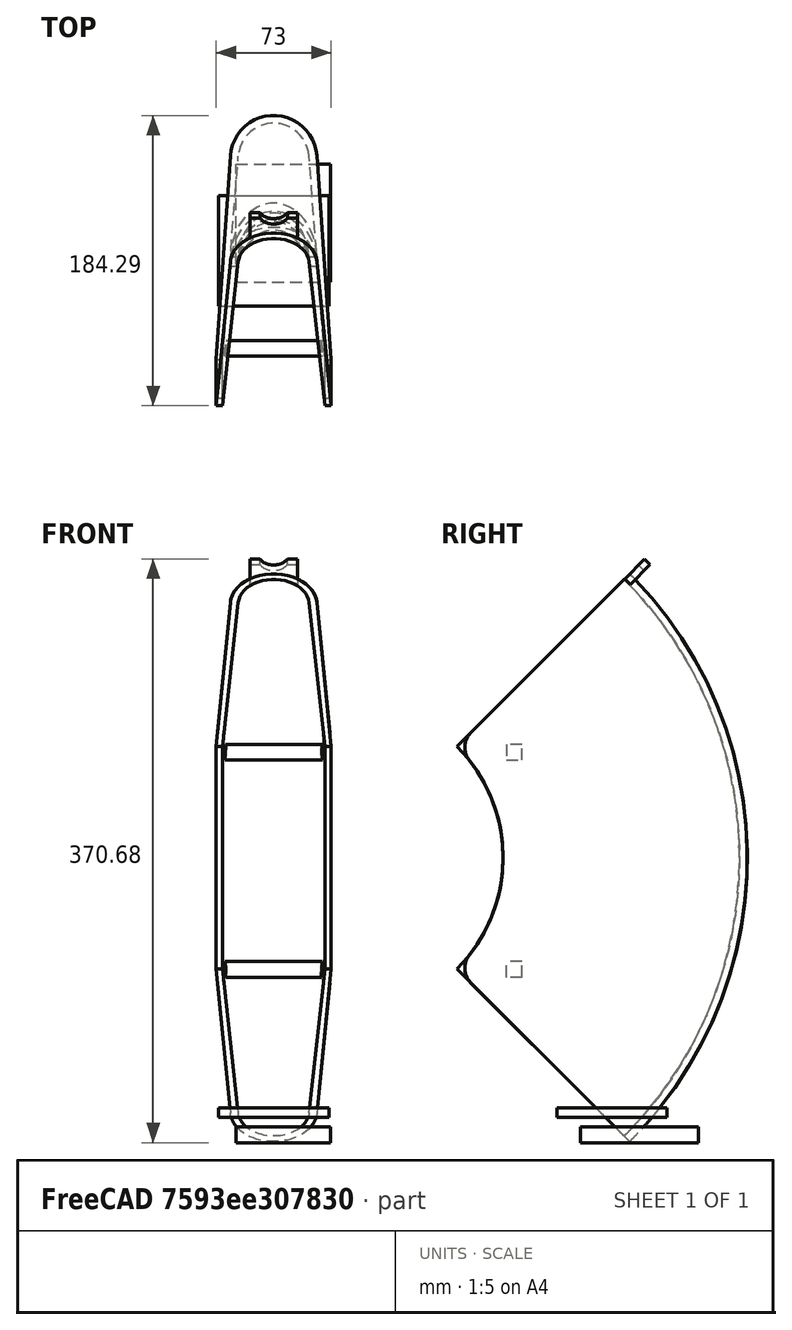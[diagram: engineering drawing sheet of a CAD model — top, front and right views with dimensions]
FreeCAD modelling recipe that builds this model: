
FCSTD DOCUMENT  (FreeCAD 0.19R)
Label: Mudguard3
License: All rights reserved
LicenseURL: http://en.wikipedia.org/wiki/All_rights_reserved
objects: Part::Box×4, Sketcher::SketchObject×3, Part::MultiFuse×3, PartDesign::Fillet×2, PartDesign::Revolution×1, PartDesign::ShapeBinder×1, PartDesign::Pad×1, PartDesign::Pocket×1, PartDesign::Body×1, Mesh::Feature×1
note: 22 computed .brp shape members not serialized (recipe doc carries the construction recipe); baked Part::Feature solids carry a one-line shape summary decoded from their .brp

FEATURE [Sketcher::SketchObject] Sketch
  FullyConstrained = false
  MapMode = 5
  Support = -> [XY_Plane]
  sketch-geometry (9):
    g0: LineSegment StartX=-38.02 StartY=255 StartZ=0 EndX=36.46 EndY=255 EndZ=0
    g1: ArcOfCircle CenterX=1e-15 CenterY=227.426 CenterZ=0 NormalX=0 NormalY=0 NormalZ=1 AngleXU=0 Radius=27.5737 StartAngle=0.0694168 EndAngle=3.07218
    g2: ArcOfCircle CenterX=0 CenterY=227.499 CenterZ=0 NormalX=0 NormalY=0 NormalZ=1 AngleXU=0 Radius=22.5673 StartAngle=0.0772218 EndAngle=3.06437
    g3: LineSegment StartX=-36.5 StartY=100 StartZ=0 EndX=-27.5073 EndY=229.339 EndZ=0
    g4: LineSegment StartX=-32.5 StartY=100 StartZ=0 EndX=-22.5 EndY=229.24 EndZ=0
    g5: LineSegment StartX=22.5 StartY=229.24 StartZ=0 EndX=32.5 EndY=100 EndZ=0
    g6: LineSegment StartX=-36.5 StartY=100 StartZ=0 EndX=-32.5 EndY=100 EndZ=0
    g7: LineSegment StartX=32.5 StartY=100 StartZ=0 EndX=36.5 EndY=100 EndZ=0
    g8: LineSegment StartX=36.5 StartY=100 StartZ=0 EndX=27.5073 EndY=229.339 EndZ=0
  constraints (23):
    c: Horizontal(g0)
    c: DistanceY(g0) = 255
    c: Tangent(g1,g0)
    c: Symmetric(g1,g1,g-2)
    c: Distance(g0) = 74.48
    c: DistanceX(g0) = 36.46
    c: Tangent(g3,g1) = 1.5708
    c: Coincident(g6,g3)
    c: Coincident(g6,g4)
    c: Distance(g6) = 4
    c: Tangent(g4,g2) = 1.5708
    c: Tangent(g5,g2) = 1.5708
    c: PointOnObject(g2,g-2)
    c: Coincident(g5,g7)
    c: Coincident(g7,g8)
    c: Coincident(g8,g1)
    c: Symmetric(g5,g4,g-2)
    c: Symmetric(g7,g3,g-2)
    c: Horizontal(g7)
    c: Distance(g5,g4) = 65
    c: Distance(g2,g2) = 45
    c: Distance(g1,g5) = 5
    c: DistanceY(g7) = 100
FEATURE [PartDesign::Revolution] Revolution
  Angle = 90
  Axis = (1,0,0)
  Base = (0,0,0)
  Midplane = true
  Profile = -> Sketch
  ReferenceAxis = -> Sketch [H_Axis]
FEATURE [Part::Box] Box  label="Cube"
  AttacherType = Attacher::AttachEngine3D
  Height = 10
  Length = 60
  Placement = pos=(-24,149,-181) rot=(0,0,1;0rad)
  Width = 75
FEATURE [Part::MultiFuse] Fusion
  Shapes = -> [Box,Revolution]
FEATURE [PartDesign::ShapeBinder] CopyFusion
  Placement = pos=(0,0,0) rot=(1,0,0;0.785398rad)
  TraceSupport = false
FEATURE [Sketcher::SketchObject] Sketch001
  FullyConstrained = true
  MapMode = 5
  Placement = pos=(0,0,0) rot=(1,0,0;0.785398rad)
  Support = -> [CopyFusion]
  sketch-geometry (6):
    g0: LineSegment StartX=-15 StartY=268.249 StartZ=0 EndX=15 EndY=268.249 EndZ=0
    g1: LineSegment StartX=15 StartY=268.249 StartZ=0 EndX=15 EndY=250.18 EndZ=0
    g2: LineSegment StartX=15 StartY=250.18 StartZ=0 EndX=-15 EndY=250.18 EndZ=0
    g3: LineSegment StartX=-15 StartY=250.18 StartZ=0 EndX=-15 EndY=268.249 EndZ=0
    g4: Circle CenterX=0 CenterY=272.75 CenterZ=0 NormalX=0 NormalY=0 NormalZ=1 AngleXU=0 Radius=9.75
    g5: LineSegment StartX=-26.66 StartY=263 StartZ=0 EndX=26.66 EndY=263 EndZ=0
  constraints (17):
    c: Coincident(g0,g1)
    c: Coincident(g1,g2)
    c: Coincident(g2,g3)
    c: Coincident(g3,g0)
    c: Horizontal(g2)
    c: Vertical(g1)
    c: Vertical(g3)
    c: Symmetric(g0,g0,g-2)
    c: Distance(g0) = 30
    c: PointOnObject(g4,g-2)
    c: Diameter(g4) = 19.5
    c: Tangent(g5,g4)
    c: DistanceY(g5) = 263
    c: DistanceY(g1) = 250.18
    c: DistanceY(g0) = 268.249
    c: Symmetric(g5,g5,g-2)
    c: Distance(g5) = 53.32
FEATURE [PartDesign::Pad] Pad
  BaseFeature = -> Revolution
  Direction = (1,1,1)
  Length = 5
  Length2 = 100
  Profile = -> Sketch001
  Reversed = true
  Type = 0
FEATURE [Sketcher::SketchObject] Sketch002
  FullyConstrained = true
  MapMode = 5
  Placement = pos=(0,-6.03e-14,6.03e-14) rot=(1,0,0;0.785398rad)
  Support = -> [Pad]
  sketch-geometry (2):
    g0: Circle CenterX=0 CenterY=272.75 CenterZ=0 NormalX=0 NormalY=0 NormalZ=1 AngleXU=0 Radius=9.75
    g1: LineSegment StartX=0 StartY=263 StartZ=0 EndX=0 EndY=255 EndZ=0
  constraints (7):
    c: PointOnObject(g0,g-2)
    c: Diameter(g0) = 19.5
    c: Vertical(g1)
    c: Distance(g1) = 8
    c: PointOnObject(g1,g0)
    c: PointOnObject(g1,g-2)
    c: DistanceY(g1) = 263
FEATURE [PartDesign::Pocket] Pocket
  BaseFeature = -> Pad
  Length = 5
  Length2 = 100
  Profile = -> Sketch002
  Type = 0
FEATURE [PartDesign::Fillet] Fillet
  Base = -> Pocket [Edge14,Edge9]
  BaseFeature = -> Pocket
  Radius = 13
  SupportTransform = false
FEATURE [PartDesign::Fillet] Fillet001
  Base = -> Fillet [Edge13,Edge7]
  BaseFeature = -> Fillet
  Radius = 13
  SupportTransform = false
FEATURE [PartDesign::Body] Body
  Group = -> [Sketch,Revolution,CopyFusion,Sketch001,Pad,Sketch002,Pocket,Fillet,Fillet001]
  Origin = -> Origin
  Tip = -> Fillet001
FEATURE [Part::Box] Box001  label="Cube001"
  AttacherType = Attacher::AttachEngine3D
  Height = 6
  Length = 70
  Placement = pos=(-35,134,-165) rot=(0,0,1;0rad)
  Width = 70
FEATURE [Part::MultiFuse] Fusion001
  Shapes = -> [Box001,Fillet001]
FEATURE [Part::Box] Box002  label="Cube002"
  AttacherType = Attacher::AttachEngine3D
  Height = 10
  Length = 67
  Placement = pos=(-34,102,-76) rot=(0,0,1;0rad)
  Width = 10
FEATURE [Part::Box] Box003  label="Cube003"
  AttacherType = Attacher::AttachEngine3D
  Height = 10
  Length = 68
  Placement = pos=(-34,102,62) rot=(0,0,1;0rad)
  Width = 10
FEATURE [Part::MultiFuse] Fusion002
  Shapes = -> [Box003,Box002,Fusion001]
FEATURE [Mesh::Feature] Mesh  label="Fusion002 (Meshed)"
